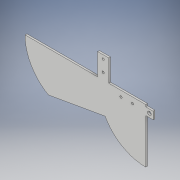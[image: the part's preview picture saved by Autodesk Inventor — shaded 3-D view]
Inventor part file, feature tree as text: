
AUTODESK INVENTOR PART (.ipt)
format: ipt  version: 2019 (Build 230136000, 136)  size: 163,328 bytes
history: native  units: in
note: dims shown in document units (in); Inventor stores cm internally (conversion verified against a paired STEP export)
features: sketch x4, extrude x3, projected_geometry x2, hole x1
ambient origin geometry x8: Origin, YZ Plane, XZ Plane, XY Plane, X Axis, Y Axis, Z Axis, Center Point
bodies: Solid1 (feature_tree)
feature tree (10):
  extrude  "Extrusion1"  Depth=3.125in
  extrude  "Extrusion2"  Depth=4.0in
  extrude  "Extrusion3"  Depth=3.125in
  hole  "Hole1"  [1 undecoded]
  sketch  "Sketch1"  dims[d0=3.125in d1=2.706in]
  sketch  "Sketch2"  dims[d2=1.563in d3=4.0in]
  sketch  "Sketch3"  dims[d4=0.0687in d5=3.125in]
  projected_geometry  "Projected Loop1"
  sketch  "Sketch4"  dims[d6=3.0in d7=0.125in d9=0.0in d10=0.0in d11=1.928in d12=0.125in d13=0.0in d14=0.5in d15=0.5in d16=3.6361in d17=0.25in d18=3.25in d19=0.25in d20=0.125in d21=0.0in d22=0.75in d23=3.5in d25=1.8516in d26=2.7285in d27=0.125in d28=0.0in d29=0.375in d30=0.25in d31=0.77in d32=0.375in d33=1.135in d35=0.0in d36=0.0in d37=0.15in d38=0.75in d39=0.375in d40=0.25in d41=0.5635in d42=1.0in d43=0.8108in d44=0.77in]
  projected_geometry  "Projected Loop2"
note: 1 required parameter value undecoded (feature->parameter linkage not recoverable at this tier; creation-order binding heuristic only, values carry confidence <= 0.55)
